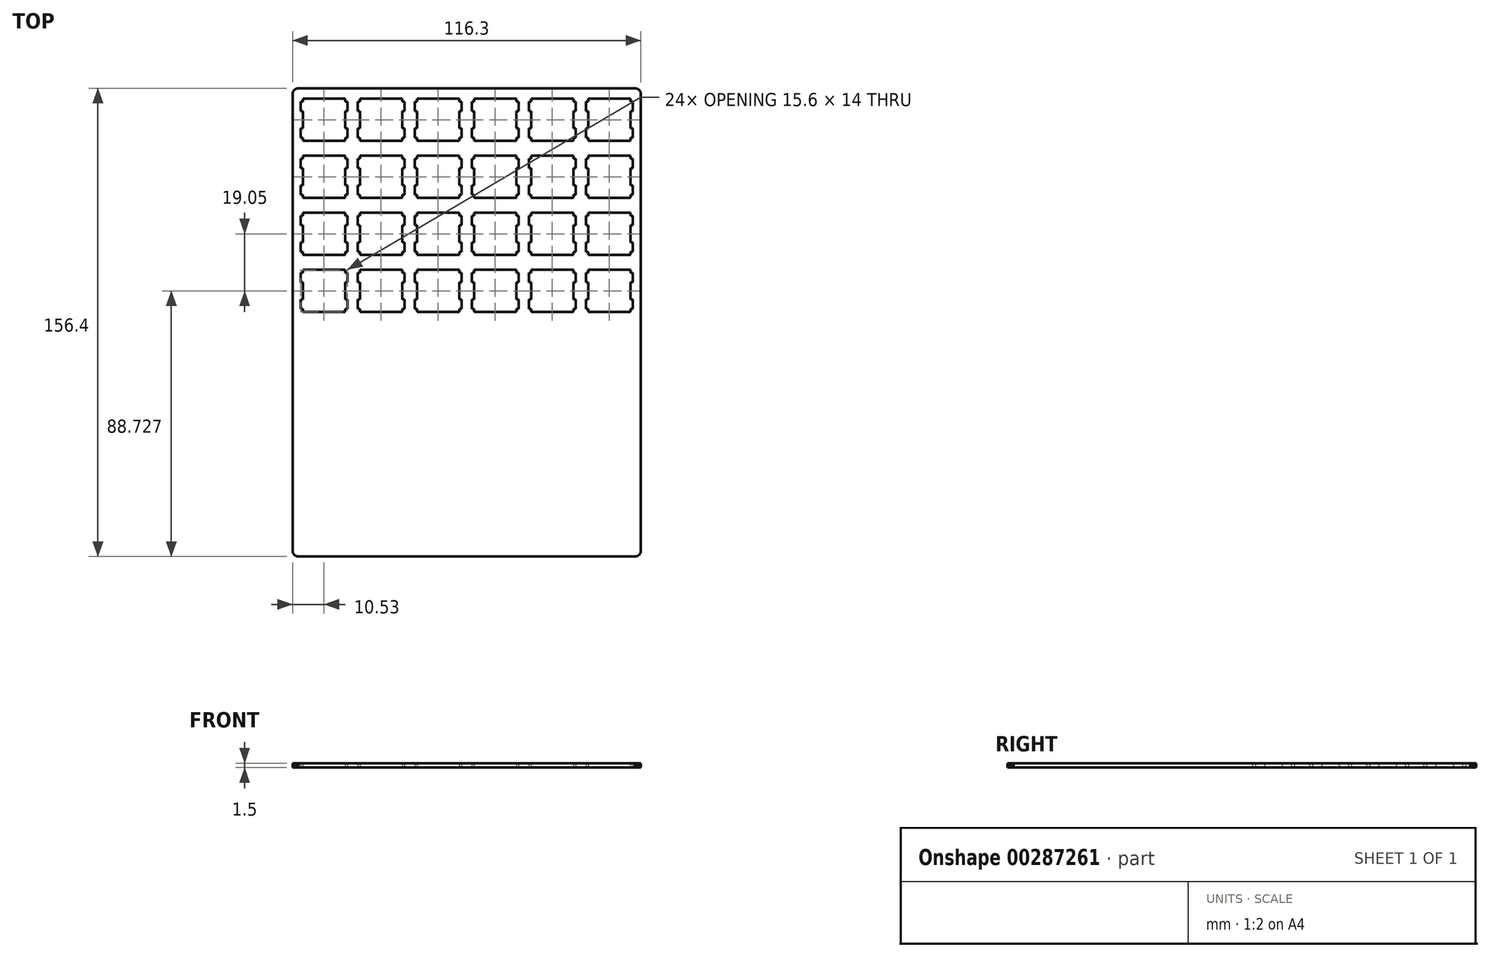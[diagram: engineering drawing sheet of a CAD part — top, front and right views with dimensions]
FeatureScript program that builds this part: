
annotation { "Feature Type Name" : "Feature", "Feature Type Description" : "" }
export const myFeature = defineFeature(function(context is Context, id is Id, definition is map)
    precondition{}
    {
        {
            var Q0;
            Q0=qCreatedBy(makeId("Top.planeOp"),FACE);
            var sketch = newSketch(context, id + "F0", { "sketchPlane" : qUnion([Q0])});
            skLineSegment(sketch, "E0", {"start": v(-39.94, 62.64) * mm, "end": v(-39.94, 61.64) * mm});
            skLineSegment(sketch, "E1", {"start": v(-39.94, 61.64) * mm, "end": v(-53.94, 61.64) * mm});
            skLineSegment(sketch, "E2", {"start": v(-53.94, 61.64) * mm, "end": v(-53.94, 62.64) * mm});
            skLineSegment(sketch, "E3", {"start": v(-53.94, 62.64) * mm, "end": v(-54.74, 62.64) * mm});
            skLineSegment(sketch, "E4", {"start": v(-54.74, 62.64) * mm, "end": v(-54.74, 65.74) * mm});
            skLineSegment(sketch, "E5", {"start": v(-54.74, 65.74) * mm, "end": v(-53.94, 65.74) * mm});
            skLineSegment(sketch, "E6", {"start": v(-53.94, 65.74) * mm, "end": v(-53.94, 71.54) * mm});
            skLineSegment(sketch, "E7", {"start": v(-53.94, 71.54) * mm, "end": v(-54.74, 71.54) * mm});
            skLineSegment(sketch, "E8", {"start": v(-54.74, 71.54) * mm, "end": v(-54.74, 74.64) * mm});
            skLineSegment(sketch, "E9", {"start": v(-54.74, 74.64) * mm, "end": v(-53.94, 74.64) * mm});
            skLineSegment(sketch, "E10", {"start": v(-53.94, 74.64) * mm, "end": v(-53.94, 75.64) * mm});
            skLineSegment(sketch, "E11", {"start": v(-53.94, 75.64) * mm, "end": v(-39.94, 75.64) * mm});
            skLineSegment(sketch, "E12", {"start": v(-39.94, 75.64) * mm, "end": v(-39.94, 74.64) * mm});
            skLineSegment(sketch, "E13", {"start": v(-39.94, 74.64) * mm, "end": v(-39.14, 74.64) * mm});
            skLineSegment(sketch, "E14", {"start": v(-39.14, 74.64) * mm, "end": v(-39.14, 71.54) * mm});
            skLineSegment(sketch, "E15", {"start": v(-39.14, 71.54) * mm, "end": v(-39.94, 71.54) * mm});
            skLineSegment(sketch, "E16", {"start": v(-39.94, 71.54) * mm, "end": v(-39.94, 65.74) * mm});
            skLineSegment(sketch, "E17", {"start": v(-39.94, 65.74) * mm, "end": v(-39.14, 65.74) * mm});
            skLineSegment(sketch, "E18", {"start": v(-39.14, 65.74) * mm, "end": v(-39.14, 62.64) * mm});
            skLineSegment(sketch, "E19", {"start": v(-39.14, 62.64) * mm, "end": v(-39.94, 62.64) * mm});
            skLineSegment(sketch, "E20", {"start": v(-39.94, 43.59) * mm, "end": v(-39.94, 42.59) * mm});
            skLineSegment(sketch, "E21", {"start": v(-39.94, 42.59) * mm, "end": v(-53.94, 42.59) * mm});
            skLineSegment(sketch, "E22", {"start": v(-53.94, 42.59) * mm, "end": v(-53.94, 43.59) * mm});
            skLineSegment(sketch, "E23", {"start": v(-53.94, 43.59) * mm, "end": v(-54.74, 43.59) * mm});
            skLineSegment(sketch, "E24", {"start": v(-54.74, 43.59) * mm, "end": v(-54.74, 46.69) * mm});
            skLineSegment(sketch, "E25", {"start": v(-54.74, 46.69) * mm, "end": v(-53.94, 46.69) * mm});
            skLineSegment(sketch, "E26", {"start": v(-53.94, 46.69) * mm, "end": v(-53.94, 52.49) * mm});
            skLineSegment(sketch, "E27", {"start": v(-53.94, 52.49) * mm, "end": v(-54.74, 52.49) * mm});
            skLineSegment(sketch, "E28", {"start": v(-54.74, 52.49) * mm, "end": v(-54.74, 55.59) * mm});
            skLineSegment(sketch, "E29", {"start": v(-54.74, 55.59) * mm, "end": v(-53.94, 55.59) * mm});
            skLineSegment(sketch, "E30", {"start": v(-53.94, 55.59) * mm, "end": v(-53.94, 56.59) * mm});
            skLineSegment(sketch, "E31", {"start": v(-53.94, 56.59) * mm, "end": v(-39.94, 56.59) * mm});
            skLineSegment(sketch, "E32", {"start": v(-39.94, 56.59) * mm, "end": v(-39.94, 55.59) * mm});
            skLineSegment(sketch, "E33", {"start": v(-39.94, 55.59) * mm, "end": v(-39.14, 55.59) * mm});
            skLineSegment(sketch, "E34", {"start": v(-39.14, 55.59) * mm, "end": v(-39.14, 52.49) * mm});
            skLineSegment(sketch, "E35", {"start": v(-39.14, 52.49) * mm, "end": v(-39.94, 52.49) * mm});
            skLineSegment(sketch, "E36", {"start": v(-39.94, 52.49) * mm, "end": v(-39.94, 46.69) * mm});
            skLineSegment(sketch, "E37", {"start": v(-39.94, 46.69) * mm, "end": v(-39.14, 46.69) * mm});
            skLineSegment(sketch, "E38", {"start": v(-39.14, 46.69) * mm, "end": v(-39.14, 43.59) * mm});
            skLineSegment(sketch, "E39", {"start": v(-39.14, 43.59) * mm, "end": v(-39.94, 43.59) * mm});
            skLineSegment(sketch, "E40", {"start": v(-39.94, 24.54) * mm, "end": v(-39.94, 23.54) * mm});
            skLineSegment(sketch, "E41", {"start": v(-39.94, 23.54) * mm, "end": v(-53.94, 23.54) * mm});
            skLineSegment(sketch, "E42", {"start": v(-53.94, 23.54) * mm, "end": v(-53.94, 24.54) * mm});
            skLineSegment(sketch, "E43", {"start": v(-53.94, 24.54) * mm, "end": v(-54.74, 24.54) * mm});
            skLineSegment(sketch, "E44", {"start": v(-54.74, 24.54) * mm, "end": v(-54.74, 27.64) * mm});
            skLineSegment(sketch, "E45", {"start": v(-54.74, 27.64) * mm, "end": v(-53.94, 27.64) * mm});
            skLineSegment(sketch, "E46", {"start": v(-53.94, 27.64) * mm, "end": v(-53.94, 33.44) * mm});
            skLineSegment(sketch, "E47", {"start": v(-53.94, 33.44) * mm, "end": v(-54.74, 33.44) * mm});
            skLineSegment(sketch, "E48", {"start": v(-54.74, 33.44) * mm, "end": v(-54.74, 36.54) * mm});
            skLineSegment(sketch, "E49", {"start": v(-54.74, 36.54) * mm, "end": v(-53.94, 36.54) * mm});
            skLineSegment(sketch, "E50", {"start": v(-53.94, 36.54) * mm, "end": v(-53.94, 37.54) * mm});
            skLineSegment(sketch, "E51", {"start": v(-53.94, 37.54) * mm, "end": v(-39.94, 37.54) * mm});
            skLineSegment(sketch, "E52", {"start": v(-39.94, 37.54) * mm, "end": v(-39.94, 36.54) * mm});
            skLineSegment(sketch, "E53", {"start": v(-39.94, 36.54) * mm, "end": v(-39.14, 36.54) * mm});
            skLineSegment(sketch, "E54", {"start": v(-39.14, 36.54) * mm, "end": v(-39.14, 33.44) * mm});
            skLineSegment(sketch, "E55", {"start": v(-39.14, 33.44) * mm, "end": v(-39.94, 33.44) * mm});
            skLineSegment(sketch, "E56", {"start": v(-39.94, 33.44) * mm, "end": v(-39.94, 27.64) * mm});
            skLineSegment(sketch, "E57", {"start": v(-39.94, 27.64) * mm, "end": v(-39.14, 27.64) * mm});
            skLineSegment(sketch, "E58", {"start": v(-39.14, 27.64) * mm, "end": v(-39.14, 24.54) * mm});
            skLineSegment(sketch, "E59", {"start": v(-39.14, 24.54) * mm, "end": v(-39.94, 24.54) * mm});
            skLineSegment(sketch, "E60", {"start": v(-39.94, 5.49) * mm, "end": v(-39.94, 4.49) * mm});
            skLineSegment(sketch, "E61", {"start": v(-39.94, 4.49) * mm, "end": v(-53.94, 4.49) * mm});
            skLineSegment(sketch, "E62", {"start": v(-53.94, 4.49) * mm, "end": v(-53.94, 5.49) * mm});
            skLineSegment(sketch, "E63", {"start": v(-53.94, 5.49) * mm, "end": v(-54.74, 5.49) * mm});
            skLineSegment(sketch, "E64", {"start": v(-54.74, 5.49) * mm, "end": v(-54.74, 8.59) * mm});
            skLineSegment(sketch, "E65", {"start": v(-54.74, 8.59) * mm, "end": v(-53.94, 8.59) * mm});
            skLineSegment(sketch, "E66", {"start": v(-53.94, 8.59) * mm, "end": v(-53.94, 14.39) * mm});
            skLineSegment(sketch, "E67", {"start": v(-53.94, 14.39) * mm, "end": v(-54.74, 14.39) * mm});
            skLineSegment(sketch, "E68", {"start": v(-54.74, 14.39) * mm, "end": v(-54.74, 17.49) * mm});
            skLineSegment(sketch, "E69", {"start": v(-54.74, 17.49) * mm, "end": v(-53.94, 17.49) * mm});
            skLineSegment(sketch, "E70", {"start": v(-53.94, 17.49) * mm, "end": v(-53.94, 18.49) * mm});
            skLineSegment(sketch, "E71", {"start": v(-53.94, 18.49) * mm, "end": v(-39.94, 18.49) * mm});
            skLineSegment(sketch, "E72", {"start": v(-39.94, 18.49) * mm, "end": v(-39.94, 17.49) * mm});
            skLineSegment(sketch, "E73", {"start": v(-39.94, 17.49) * mm, "end": v(-39.14, 17.49) * mm});
            skLineSegment(sketch, "E74", {"start": v(-39.14, 17.49) * mm, "end": v(-39.14, 14.39) * mm});
            skLineSegment(sketch, "E75", {"start": v(-39.14, 14.39) * mm, "end": v(-39.94, 14.39) * mm});
            skLineSegment(sketch, "E76", {"start": v(-39.94, 14.39) * mm, "end": v(-39.94, 8.59) * mm});
            skLineSegment(sketch, "E77", {"start": v(-39.94, 8.59) * mm, "end": v(-39.14, 8.59) * mm});
            skLineSegment(sketch, "E78", {"start": v(-39.14, 8.59) * mm, "end": v(-39.14, 5.49) * mm});
            skLineSegment(sketch, "E79", {"start": v(-39.14, 5.49) * mm, "end": v(-39.94, 5.49) * mm});
            skLineSegment(sketch, "E80", {"start": v(-20.9, 62.64) * mm, "end": v(-20.9, 61.64) * mm});
            skLineSegment(sketch, "E81", {"start": v(-20.9, 61.64) * mm, "end": v(-34.9, 61.64) * mm});
            skLineSegment(sketch, "E82", {"start": v(-34.9, 61.64) * mm, "end": v(-34.9, 62.64) * mm});
            skLineSegment(sketch, "E83", {"start": v(-34.9, 62.64) * mm, "end": v(-35.7, 62.64) * mm});
            skLineSegment(sketch, "E84", {"start": v(-35.7, 62.64) * mm, "end": v(-35.7, 65.74) * mm});
            skLineSegment(sketch, "E85", {"start": v(-35.7, 65.74) * mm, "end": v(-34.9, 65.74) * mm});
            skLineSegment(sketch, "E86", {"start": v(-34.9, 65.74) * mm, "end": v(-34.9, 71.54) * mm});
            skLineSegment(sketch, "E87", {"start": v(-34.9, 71.54) * mm, "end": v(-35.7, 71.54) * mm});
            skLineSegment(sketch, "E88", {"start": v(-35.7, 71.54) * mm, "end": v(-35.7, 74.64) * mm});
            skLineSegment(sketch, "E89", {"start": v(-35.7, 74.64) * mm, "end": v(-34.9, 74.64) * mm});
            skLineSegment(sketch, "E90", {"start": v(-34.9, 74.64) * mm, "end": v(-34.9, 75.64) * mm});
            skLineSegment(sketch, "E91", {"start": v(-34.9, 75.64) * mm, "end": v(-20.9, 75.64) * mm});
            skLineSegment(sketch, "E92", {"start": v(-20.9, 75.64) * mm, "end": v(-20.9, 74.64) * mm});
            skLineSegment(sketch, "E93", {"start": v(-20.9, 74.64) * mm, "end": v(-20.1, 74.64) * mm});
            skLineSegment(sketch, "E94", {"start": v(-20.1, 74.64) * mm, "end": v(-20.1, 71.54) * mm});
            skLineSegment(sketch, "E95", {"start": v(-20.1, 71.54) * mm, "end": v(-20.9, 71.54) * mm});
            skLineSegment(sketch, "E96", {"start": v(-20.9, 71.54) * mm, "end": v(-20.9, 65.74) * mm});
            skLineSegment(sketch, "E97", {"start": v(-20.9, 65.74) * mm, "end": v(-20.1, 65.74) * mm});
            skLineSegment(sketch, "E98", {"start": v(-20.1, 65.74) * mm, "end": v(-20.1, 62.64) * mm});
            skLineSegment(sketch, "E99", {"start": v(-20.1, 62.64) * mm, "end": v(-20.9, 62.64) * mm});
            skLineSegment(sketch, "E100", {"start": v(-20.9, 43.59) * mm, "end": v(-20.9, 42.59) * mm});
            skLineSegment(sketch, "E101", {"start": v(-20.9, 42.59) * mm, "end": v(-34.9, 42.59) * mm});
            skLineSegment(sketch, "E102", {"start": v(-34.9, 42.59) * mm, "end": v(-34.9, 43.59) * mm});
            skLineSegment(sketch, "E103", {"start": v(-34.9, 43.59) * mm, "end": v(-35.7, 43.59) * mm});
            skLineSegment(sketch, "E104", {"start": v(-35.7, 43.59) * mm, "end": v(-35.7, 46.69) * mm});
            skLineSegment(sketch, "E105", {"start": v(-35.7, 46.69) * mm, "end": v(-34.9, 46.69) * mm});
            skLineSegment(sketch, "E106", {"start": v(-34.9, 46.69) * mm, "end": v(-34.9, 52.49) * mm});
            skLineSegment(sketch, "E107", {"start": v(-34.9, 52.49) * mm, "end": v(-35.7, 52.49) * mm});
            skLineSegment(sketch, "E108", {"start": v(-35.7, 52.49) * mm, "end": v(-35.7, 55.59) * mm});
            skLineSegment(sketch, "E109", {"start": v(-35.7, 55.59) * mm, "end": v(-34.9, 55.59) * mm});
            skLineSegment(sketch, "E110", {"start": v(-34.9, 55.59) * mm, "end": v(-34.9, 56.59) * mm});
            skLineSegment(sketch, "E111", {"start": v(-34.9, 56.59) * mm, "end": v(-20.9, 56.59) * mm});
            skLineSegment(sketch, "E112", {"start": v(-20.9, 56.59) * mm, "end": v(-20.9, 55.59) * mm});
            skLineSegment(sketch, "E113", {"start": v(-20.9, 55.59) * mm, "end": v(-20.1, 55.59) * mm});
            skLineSegment(sketch, "E114", {"start": v(-20.1, 55.59) * mm, "end": v(-20.1, 52.49) * mm});
            skLineSegment(sketch, "E115", {"start": v(-20.1, 52.49) * mm, "end": v(-20.9, 52.49) * mm});
            skLineSegment(sketch, "E116", {"start": v(-20.9, 52.49) * mm, "end": v(-20.9, 46.69) * mm});
            skLineSegment(sketch, "E117", {"start": v(-20.9, 46.69) * mm, "end": v(-20.1, 46.69) * mm});
            skLineSegment(sketch, "E118", {"start": v(-20.1, 46.69) * mm, "end": v(-20.1, 43.59) * mm});
            skLineSegment(sketch, "E119", {"start": v(-20.1, 43.59) * mm, "end": v(-20.9, 43.59) * mm});
            skLineSegment(sketch, "E120", {"start": v(-20.9, 24.54) * mm, "end": v(-20.9, 23.54) * mm});
            skLineSegment(sketch, "E121", {"start": v(-20.9, 23.54) * mm, "end": v(-34.9, 23.54) * mm});
            skLineSegment(sketch, "E122", {"start": v(-34.9, 23.54) * mm, "end": v(-34.9, 24.54) * mm});
            skLineSegment(sketch, "E123", {"start": v(-34.9, 24.54) * mm, "end": v(-35.7, 24.54) * mm});
            skLineSegment(sketch, "E124", {"start": v(-35.7, 24.54) * mm, "end": v(-35.7, 27.64) * mm});
            skLineSegment(sketch, "E125", {"start": v(-35.7, 27.64) * mm, "end": v(-34.9, 27.64) * mm});
            skLineSegment(sketch, "E126", {"start": v(-34.9, 27.64) * mm, "end": v(-34.9, 33.44) * mm});
            skLineSegment(sketch, "E127", {"start": v(-34.9, 33.44) * mm, "end": v(-35.7, 33.44) * mm});
            skLineSegment(sketch, "E128", {"start": v(-35.7, 33.44) * mm, "end": v(-35.7, 36.54) * mm});
            skLineSegment(sketch, "E129", {"start": v(-35.7, 36.54) * mm, "end": v(-34.9, 36.54) * mm});
            skLineSegment(sketch, "E130", {"start": v(-34.9, 36.54) * mm, "end": v(-34.9, 37.54) * mm});
            skLineSegment(sketch, "E131", {"start": v(-34.9, 37.54) * mm, "end": v(-20.9, 37.54) * mm});
            skLineSegment(sketch, "E132", {"start": v(-20.9, 37.54) * mm, "end": v(-20.9, 36.54) * mm});
            skLineSegment(sketch, "E133", {"start": v(-20.9, 36.54) * mm, "end": v(-20.1, 36.54) * mm});
            skLineSegment(sketch, "E134", {"start": v(-20.1, 36.54) * mm, "end": v(-20.1, 33.44) * mm});
            skLineSegment(sketch, "E135", {"start": v(-20.1, 33.44) * mm, "end": v(-20.9, 33.44) * mm});
            skLineSegment(sketch, "E136", {"start": v(-20.9, 33.44) * mm, "end": v(-20.9, 27.64) * mm});
            skLineSegment(sketch, "E137", {"start": v(-20.9, 27.64) * mm, "end": v(-20.1, 27.64) * mm});
            skLineSegment(sketch, "E138", {"start": v(-20.1, 27.64) * mm, "end": v(-20.1, 24.54) * mm});
            skLineSegment(sketch, "E139", {"start": v(-20.1, 24.54) * mm, "end": v(-20.9, 24.54) * mm});
            skLineSegment(sketch, "E140", {"start": v(-20.9, 5.49) * mm, "end": v(-20.9, 4.49) * mm});
            skLineSegment(sketch, "E141", {"start": v(-20.9, 4.49) * mm, "end": v(-34.9, 4.49) * mm});
            skLineSegment(sketch, "E142", {"start": v(-34.9, 4.49) * mm, "end": v(-34.9, 5.49) * mm});
            skLineSegment(sketch, "E143", {"start": v(-34.9, 5.49) * mm, "end": v(-35.7, 5.49) * mm});
            skLineSegment(sketch, "E144", {"start": v(-35.7, 5.49) * mm, "end": v(-35.7, 8.59) * mm});
            skLineSegment(sketch, "E145", {"start": v(-35.7, 8.59) * mm, "end": v(-34.9, 8.59) * mm});
            skLineSegment(sketch, "E146", {"start": v(-34.9, 8.59) * mm, "end": v(-34.9, 14.39) * mm});
            skLineSegment(sketch, "E147", {"start": v(-34.9, 14.39) * mm, "end": v(-35.7, 14.39) * mm});
            skLineSegment(sketch, "E148", {"start": v(-35.7, 14.39) * mm, "end": v(-35.7, 17.49) * mm});
            skLineSegment(sketch, "E149", {"start": v(-35.7, 17.49) * mm, "end": v(-34.9, 17.49) * mm});
            skLineSegment(sketch, "E150", {"start": v(-34.9, 17.49) * mm, "end": v(-34.9, 18.49) * mm});
            skLineSegment(sketch, "E151", {"start": v(-34.9, 18.49) * mm, "end": v(-20.9, 18.49) * mm});
            skLineSegment(sketch, "E152", {"start": v(-20.9, 18.49) * mm, "end": v(-20.9, 17.49) * mm});
            skLineSegment(sketch, "E153", {"start": v(-20.9, 17.49) * mm, "end": v(-20.1, 17.49) * mm});
            skLineSegment(sketch, "E154", {"start": v(-20.1, 17.49) * mm, "end": v(-20.1, 14.39) * mm});
            skLineSegment(sketch, "E155", {"start": v(-20.1, 14.39) * mm, "end": v(-20.9, 14.39) * mm});
            skLineSegment(sketch, "E156", {"start": v(-20.9, 14.39) * mm, "end": v(-20.9, 8.59) * mm});
            skLineSegment(sketch, "E157", {"start": v(-20.9, 8.59) * mm, "end": v(-20.1, 8.59) * mm});
            skLineSegment(sketch, "E158", {"start": v(-20.1, 8.59) * mm, "end": v(-20.1, 5.49) * mm});
            skLineSegment(sketch, "E159", {"start": v(-20.1, 5.49) * mm, "end": v(-20.9, 5.49) * mm});
            skLineSegment(sketch, "E160", {"start": v(-1.84, 62.64) * mm, "end": v(-1.84, 61.64) * mm});
            skLineSegment(sketch, "E161", {"start": v(-1.84, 61.64) * mm, "end": v(-15.84, 61.64) * mm});
            skLineSegment(sketch, "E162", {"start": v(-15.84, 61.64) * mm, "end": v(-15.84, 62.64) * mm});
            skLineSegment(sketch, "E163", {"start": v(-15.84, 62.64) * mm, "end": v(-16.64, 62.64) * mm});
            skLineSegment(sketch, "E164", {"start": v(-16.64, 62.64) * mm, "end": v(-16.64, 65.74) * mm});
            skLineSegment(sketch, "E165", {"start": v(-16.64, 65.74) * mm, "end": v(-15.84, 65.74) * mm});
            skLineSegment(sketch, "E166", {"start": v(-15.84, 65.74) * mm, "end": v(-15.84, 71.54) * mm});
            skLineSegment(sketch, "E167", {"start": v(-15.84, 71.54) * mm, "end": v(-16.64, 71.54) * mm});
            skLineSegment(sketch, "E168", {"start": v(-16.64, 71.54) * mm, "end": v(-16.64, 74.64) * mm});
            skLineSegment(sketch, "E169", {"start": v(-16.64, 74.64) * mm, "end": v(-15.84, 74.64) * mm});
            skLineSegment(sketch, "E170", {"start": v(-15.84, 74.64) * mm, "end": v(-15.84, 75.64) * mm});
            skLineSegment(sketch, "E171", {"start": v(-15.84, 75.64) * mm, "end": v(-1.84, 75.64) * mm});
            skLineSegment(sketch, "E172", {"start": v(-1.84, 75.64) * mm, "end": v(-1.84, 74.64) * mm});
            skLineSegment(sketch, "E173", {"start": v(-1.84, 74.64) * mm, "end": v(-1.04, 74.64) * mm});
            skLineSegment(sketch, "E174", {"start": v(-1.04, 74.64) * mm, "end": v(-1.04, 71.54) * mm});
            skLineSegment(sketch, "E175", {"start": v(-1.04, 71.54) * mm, "end": v(-1.84, 71.54) * mm});
            skLineSegment(sketch, "E176", {"start": v(-1.84, 71.54) * mm, "end": v(-1.84, 65.74) * mm});
            skLineSegment(sketch, "E177", {"start": v(-1.84, 65.74) * mm, "end": v(-1.04, 65.74) * mm});
            skLineSegment(sketch, "E178", {"start": v(-1.04, 65.74) * mm, "end": v(-1.04, 62.64) * mm});
            skLineSegment(sketch, "E179", {"start": v(-1.04, 62.64) * mm, "end": v(-1.84, 62.64) * mm});
            skLineSegment(sketch, "E180", {"start": v(-1.84, 43.59) * mm, "end": v(-1.84, 42.59) * mm});
            skLineSegment(sketch, "E181", {"start": v(-1.84, 42.59) * mm, "end": v(-15.84, 42.59) * mm});
            skLineSegment(sketch, "E182", {"start": v(-15.84, 42.59) * mm, "end": v(-15.84, 43.59) * mm});
            skLineSegment(sketch, "E183", {"start": v(-15.84, 43.59) * mm, "end": v(-16.64, 43.59) * mm});
            skLineSegment(sketch, "E184", {"start": v(-16.64, 43.59) * mm, "end": v(-16.64, 46.69) * mm});
            skLineSegment(sketch, "E185", {"start": v(-16.64, 46.69) * mm, "end": v(-15.84, 46.69) * mm});
            skLineSegment(sketch, "E186", {"start": v(-15.84, 46.69) * mm, "end": v(-15.84, 52.49) * mm});
            skLineSegment(sketch, "E187", {"start": v(-15.84, 52.49) * mm, "end": v(-16.64, 52.49) * mm});
            skLineSegment(sketch, "E188", {"start": v(-16.64, 52.49) * mm, "end": v(-16.64, 55.59) * mm});
            skLineSegment(sketch, "E189", {"start": v(-16.64, 55.59) * mm, "end": v(-15.84, 55.59) * mm});
            skLineSegment(sketch, "E190", {"start": v(-15.84, 55.59) * mm, "end": v(-15.84, 56.59) * mm});
            skLineSegment(sketch, "E191", {"start": v(-15.84, 56.59) * mm, "end": v(-1.84, 56.59) * mm});
            skLineSegment(sketch, "E192", {"start": v(-1.84, 56.59) * mm, "end": v(-1.84, 55.59) * mm});
            skLineSegment(sketch, "E193", {"start": v(-1.84, 55.59) * mm, "end": v(-1.04, 55.59) * mm});
            skLineSegment(sketch, "E194", {"start": v(-1.04, 55.59) * mm, "end": v(-1.04, 52.49) * mm});
            skLineSegment(sketch, "E195", {"start": v(-1.04, 52.49) * mm, "end": v(-1.84, 52.49) * mm});
            skLineSegment(sketch, "E196", {"start": v(-1.84, 52.49) * mm, "end": v(-1.84, 46.69) * mm});
            skLineSegment(sketch, "E197", {"start": v(-1.84, 46.69) * mm, "end": v(-1.04, 46.69) * mm});
            skLineSegment(sketch, "E198", {"start": v(-1.04, 46.69) * mm, "end": v(-1.04, 43.59) * mm});
            skLineSegment(sketch, "E199", {"start": v(-1.04, 43.59) * mm, "end": v(-1.84, 43.59) * mm});
            skLineSegment(sketch, "E200", {"start": v(-1.84, 24.54) * mm, "end": v(-1.84, 23.54) * mm});
            skLineSegment(sketch, "E201", {"start": v(-1.84, 23.54) * mm, "end": v(-15.84, 23.54) * mm});
            skLineSegment(sketch, "E202", {"start": v(-15.84, 23.54) * mm, "end": v(-15.84, 24.54) * mm});
            skLineSegment(sketch, "E203", {"start": v(-15.84, 24.54) * mm, "end": v(-16.64, 24.54) * mm});
            skLineSegment(sketch, "E204", {"start": v(-16.64, 24.54) * mm, "end": v(-16.64, 27.64) * mm});
            skLineSegment(sketch, "E205", {"start": v(-16.64, 27.64) * mm, "end": v(-15.84, 27.64) * mm});
            skLineSegment(sketch, "E206", {"start": v(-15.84, 27.64) * mm, "end": v(-15.84, 33.44) * mm});
            skLineSegment(sketch, "E207", {"start": v(-15.84, 33.44) * mm, "end": v(-16.64, 33.44) * mm});
            skLineSegment(sketch, "E208", {"start": v(-16.64, 33.44) * mm, "end": v(-16.64, 36.54) * mm});
            skLineSegment(sketch, "E209", {"start": v(-16.64, 36.54) * mm, "end": v(-15.84, 36.54) * mm});
            skLineSegment(sketch, "E210", {"start": v(-15.84, 36.54) * mm, "end": v(-15.84, 37.54) * mm});
            skLineSegment(sketch, "E211", {"start": v(-15.84, 37.54) * mm, "end": v(-1.84, 37.54) * mm});
            skLineSegment(sketch, "E212", {"start": v(-1.84, 37.54) * mm, "end": v(-1.84, 36.54) * mm});
            skLineSegment(sketch, "E213", {"start": v(-1.84, 36.54) * mm, "end": v(-1.04, 36.54) * mm});
            skLineSegment(sketch, "E214", {"start": v(-1.04, 36.54) * mm, "end": v(-1.04, 33.44) * mm});
            skLineSegment(sketch, "E215", {"start": v(-1.04, 33.44) * mm, "end": v(-1.84, 33.44) * mm});
            skLineSegment(sketch, "E216", {"start": v(-1.84, 33.44) * mm, "end": v(-1.84, 27.64) * mm});
            skLineSegment(sketch, "E217", {"start": v(-1.84, 27.64) * mm, "end": v(-1.04, 27.64) * mm});
            skLineSegment(sketch, "E218", {"start": v(-1.04, 27.64) * mm, "end": v(-1.04, 24.54) * mm});
            skLineSegment(sketch, "E219", {"start": v(-1.04, 24.54) * mm, "end": v(-1.84, 24.54) * mm});
            skLineSegment(sketch, "E220", {"start": v(-1.84, 5.49) * mm, "end": v(-1.84, 4.49) * mm});
            skLineSegment(sketch, "E221", {"start": v(-1.84, 4.49) * mm, "end": v(-15.84, 4.49) * mm});
            skLineSegment(sketch, "E222", {"start": v(-15.84, 4.49) * mm, "end": v(-15.84, 5.49) * mm});
            skLineSegment(sketch, "E223", {"start": v(-15.84, 5.49) * mm, "end": v(-16.64, 5.49) * mm});
            skLineSegment(sketch, "E224", {"start": v(-16.64, 5.49) * mm, "end": v(-16.64, 8.59) * mm});
            skLineSegment(sketch, "E225", {"start": v(-16.64, 8.59) * mm, "end": v(-15.84, 8.59) * mm});
            skLineSegment(sketch, "E226", {"start": v(-15.84, 8.59) * mm, "end": v(-15.84, 14.39) * mm});
            skLineSegment(sketch, "E227", {"start": v(-15.84, 14.39) * mm, "end": v(-16.64, 14.39) * mm});
            skLineSegment(sketch, "E228", {"start": v(-16.64, 14.39) * mm, "end": v(-16.64, 17.49) * mm});
            skLineSegment(sketch, "E229", {"start": v(-16.64, 17.49) * mm, "end": v(-15.84, 17.49) * mm});
            skLineSegment(sketch, "E230", {"start": v(-15.84, 17.49) * mm, "end": v(-15.84, 18.49) * mm});
            skLineSegment(sketch, "E231", {"start": v(-15.84, 18.49) * mm, "end": v(-1.84, 18.49) * mm});
            skLineSegment(sketch, "E232", {"start": v(-1.84, 18.49) * mm, "end": v(-1.84, 17.49) * mm});
            skLineSegment(sketch, "E233", {"start": v(-1.84, 17.49) * mm, "end": v(-1.04, 17.49) * mm});
            skLineSegment(sketch, "E234", {"start": v(-1.04, 17.49) * mm, "end": v(-1.04, 14.39) * mm});
            skLineSegment(sketch, "E235", {"start": v(-1.04, 14.39) * mm, "end": v(-1.84, 14.39) * mm});
            skLineSegment(sketch, "E236", {"start": v(-1.84, 14.39) * mm, "end": v(-1.84, 8.59) * mm});
            skLineSegment(sketch, "E237", {"start": v(-1.84, 8.59) * mm, "end": v(-1.04, 8.59) * mm});
            skLineSegment(sketch, "E238", {"start": v(-1.04, 8.59) * mm, "end": v(-1.04, 5.49) * mm});
            skLineSegment(sketch, "E239", {"start": v(-1.04, 5.49) * mm, "end": v(-1.84, 5.49) * mm});
            skLineSegment(sketch, "E240", {"start": v(17.2, 62.64) * mm, "end": v(17.2, 61.64) * mm});
            skLineSegment(sketch, "E241", {"start": v(17.2, 61.64) * mm, "end": v(3.2, 61.64) * mm});
            skLineSegment(sketch, "E242", {"start": v(3.2, 61.64) * mm, "end": v(3.2, 62.64) * mm});
            skLineSegment(sketch, "E243", {"start": v(3.2, 62.64) * mm, "end": v(2.4, 62.64) * mm});
            skLineSegment(sketch, "E244", {"start": v(2.4, 62.64) * mm, "end": v(2.4, 65.74) * mm});
            skLineSegment(sketch, "E245", {"start": v(2.4, 65.74) * mm, "end": v(3.2, 65.74) * mm});
            skLineSegment(sketch, "E246", {"start": v(3.2, 65.74) * mm, "end": v(3.2, 71.54) * mm});
            skLineSegment(sketch, "E247", {"start": v(3.2, 71.54) * mm, "end": v(2.4, 71.54) * mm});
            skLineSegment(sketch, "E248", {"start": v(2.4, 71.54) * mm, "end": v(2.4, 74.64) * mm});
            skLineSegment(sketch, "E249", {"start": v(2.4, 74.64) * mm, "end": v(3.2, 74.64) * mm});
            skLineSegment(sketch, "E250", {"start": v(3.2, 74.64) * mm, "end": v(3.2, 75.64) * mm});
            skLineSegment(sketch, "E251", {"start": v(3.2, 75.64) * mm, "end": v(17.2, 75.64) * mm});
            skLineSegment(sketch, "E252", {"start": v(17.2, 75.64) * mm, "end": v(17.2, 74.64) * mm});
            skLineSegment(sketch, "E253", {"start": v(17.2, 74.64) * mm, "end": v(18, 74.64) * mm});
            skLineSegment(sketch, "E254", {"start": v(18, 74.64) * mm, "end": v(18, 71.54) * mm});
            skLineSegment(sketch, "E255", {"start": v(18, 71.54) * mm, "end": v(17.2, 71.54) * mm});
            skLineSegment(sketch, "E256", {"start": v(17.2, 71.54) * mm, "end": v(17.2, 65.74) * mm});
            skLineSegment(sketch, "E257", {"start": v(17.2, 65.74) * mm, "end": v(18, 65.74) * mm});
            skLineSegment(sketch, "E258", {"start": v(18, 65.74) * mm, "end": v(18, 62.64) * mm});
            skLineSegment(sketch, "E259", {"start": v(18, 62.64) * mm, "end": v(17.2, 62.64) * mm});
            skLineSegment(sketch, "E260", {"start": v(17.2, 43.59) * mm, "end": v(17.2, 42.59) * mm});
            skLineSegment(sketch, "E261", {"start": v(17.2, 42.59) * mm, "end": v(3.2, 42.59) * mm});
            skLineSegment(sketch, "E262", {"start": v(3.2, 42.59) * mm, "end": v(3.2, 43.59) * mm});
            skLineSegment(sketch, "E263", {"start": v(3.2, 43.59) * mm, "end": v(2.4, 43.59) * mm});
            skLineSegment(sketch, "E264", {"start": v(2.4, 43.59) * mm, "end": v(2.4, 46.69) * mm});
            skLineSegment(sketch, "E265", {"start": v(2.4, 46.69) * mm, "end": v(3.2, 46.69) * mm});
            skLineSegment(sketch, "E266", {"start": v(3.2, 46.69) * mm, "end": v(3.2, 52.49) * mm});
            skLineSegment(sketch, "E267", {"start": v(3.2, 52.49) * mm, "end": v(2.4, 52.49) * mm});
            skLineSegment(sketch, "E268", {"start": v(2.4, 52.49) * mm, "end": v(2.4, 55.59) * mm});
            skLineSegment(sketch, "E269", {"start": v(2.4, 55.59) * mm, "end": v(3.2, 55.59) * mm});
            skLineSegment(sketch, "E270", {"start": v(3.2, 55.59) * mm, "end": v(3.2, 56.59) * mm});
            skLineSegment(sketch, "E271", {"start": v(3.2, 56.59) * mm, "end": v(17.2, 56.59) * mm});
            skLineSegment(sketch, "E272", {"start": v(17.2, 56.59) * mm, "end": v(17.2, 55.59) * mm});
            skLineSegment(sketch, "E273", {"start": v(17.2, 55.59) * mm, "end": v(18, 55.59) * mm});
            skLineSegment(sketch, "E274", {"start": v(18, 55.59) * mm, "end": v(18, 52.49) * mm});
            skLineSegment(sketch, "E275", {"start": v(18, 52.49) * mm, "end": v(17.2, 52.49) * mm});
            skLineSegment(sketch, "E276", {"start": v(17.2, 52.49) * mm, "end": v(17.2, 46.69) * mm});
            skLineSegment(sketch, "E277", {"start": v(17.2, 46.69) * mm, "end": v(18, 46.69) * mm});
            skLineSegment(sketch, "E278", {"start": v(18, 46.69) * mm, "end": v(18, 43.59) * mm});
            skLineSegment(sketch, "E279", {"start": v(18, 43.59) * mm, "end": v(17.2, 43.59) * mm});
            skLineSegment(sketch, "E280", {"start": v(17.2, 24.54) * mm, "end": v(17.2, 23.54) * mm});
            skLineSegment(sketch, "E281", {"start": v(17.2, 23.54) * mm, "end": v(3.2, 23.54) * mm});
            skLineSegment(sketch, "E282", {"start": v(3.2, 23.54) * mm, "end": v(3.2, 24.54) * mm});
            skLineSegment(sketch, "E283", {"start": v(3.2, 24.54) * mm, "end": v(2.4, 24.54) * mm});
            skLineSegment(sketch, "E284", {"start": v(2.4, 24.54) * mm, "end": v(2.4, 27.64) * mm});
            skLineSegment(sketch, "E285", {"start": v(2.4, 27.64) * mm, "end": v(3.2, 27.64) * mm});
            skLineSegment(sketch, "E286", {"start": v(3.2, 27.64) * mm, "end": v(3.2, 33.44) * mm});
            skLineSegment(sketch, "E287", {"start": v(3.2, 33.44) * mm, "end": v(2.4, 33.44) * mm});
            skLineSegment(sketch, "E288", {"start": v(2.4, 33.44) * mm, "end": v(2.4, 36.54) * mm});
            skLineSegment(sketch, "E289", {"start": v(2.4, 36.54) * mm, "end": v(3.2, 36.54) * mm});
            skLineSegment(sketch, "E290", {"start": v(3.2, 36.54) * mm, "end": v(3.2, 37.54) * mm});
            skLineSegment(sketch, "E291", {"start": v(3.2, 37.54) * mm, "end": v(17.2, 37.54) * mm});
            skLineSegment(sketch, "E292", {"start": v(17.2, 37.54) * mm, "end": v(17.2, 36.54) * mm});
            skLineSegment(sketch, "E293", {"start": v(17.2, 36.54) * mm, "end": v(18, 36.54) * mm});
            skLineSegment(sketch, "E294", {"start": v(18, 36.54) * mm, "end": v(18, 33.44) * mm});
            skLineSegment(sketch, "E295", {"start": v(18, 33.44) * mm, "end": v(17.2, 33.44) * mm});
            skLineSegment(sketch, "E296", {"start": v(17.2, 33.44) * mm, "end": v(17.2, 27.64) * mm});
            skLineSegment(sketch, "E297", {"start": v(17.2, 27.64) * mm, "end": v(18, 27.64) * mm});
            skLineSegment(sketch, "E298", {"start": v(18, 27.64) * mm, "end": v(18, 24.54) * mm});
            skLineSegment(sketch, "E299", {"start": v(18, 24.54) * mm, "end": v(17.2, 24.54) * mm});
            skLineSegment(sketch, "E300", {"start": v(17.2, 5.49) * mm, "end": v(17.2, 4.49) * mm});
            skLineSegment(sketch, "E301", {"start": v(17.2, 4.49) * mm, "end": v(3.2, 4.49) * mm});
            skLineSegment(sketch, "E302", {"start": v(3.2, 4.49) * mm, "end": v(3.2, 5.49) * mm});
            skLineSegment(sketch, "E303", {"start": v(3.2, 5.49) * mm, "end": v(2.4, 5.49) * mm});
            skLineSegment(sketch, "E304", {"start": v(2.4, 5.49) * mm, "end": v(2.4, 8.59) * mm});
            skLineSegment(sketch, "E305", {"start": v(2.4, 8.59) * mm, "end": v(3.2, 8.59) * mm});
            skLineSegment(sketch, "E306", {"start": v(3.2, 8.59) * mm, "end": v(3.2, 14.39) * mm});
            skLineSegment(sketch, "E307", {"start": v(3.2, 14.39) * mm, "end": v(2.4, 14.39) * mm});
            skLineSegment(sketch, "E308", {"start": v(2.4, 14.39) * mm, "end": v(2.4, 17.49) * mm});
            skLineSegment(sketch, "E309", {"start": v(2.4, 17.49) * mm, "end": v(3.2, 17.49) * mm});
            skLineSegment(sketch, "E310", {"start": v(3.2, 17.49) * mm, "end": v(3.2, 18.49) * mm});
            skLineSegment(sketch, "E311", {"start": v(3.2, 18.49) * mm, "end": v(17.2, 18.49) * mm});
            skLineSegment(sketch, "E312", {"start": v(17.2, 18.49) * mm, "end": v(17.2, 17.49) * mm});
            skLineSegment(sketch, "E313", {"start": v(17.2, 17.49) * mm, "end": v(18, 17.49) * mm});
            skLineSegment(sketch, "E314", {"start": v(18, 17.49) * mm, "end": v(18, 14.39) * mm});
            skLineSegment(sketch, "E315", {"start": v(18, 14.39) * mm, "end": v(17.2, 14.39) * mm});
            skLineSegment(sketch, "E316", {"start": v(17.2, 14.39) * mm, "end": v(17.2, 8.59) * mm});
            skLineSegment(sketch, "E317", {"start": v(17.2, 8.59) * mm, "end": v(18, 8.59) * mm});
            skLineSegment(sketch, "E318", {"start": v(18, 8.59) * mm, "end": v(18, 5.49) * mm});
            skLineSegment(sketch, "E319", {"start": v(18, 5.49) * mm, "end": v(17.2, 5.49) * mm});
            skLineSegment(sketch, "E320", {"start": v(36.26, 62.64) * mm, "end": v(36.26, 61.64) * mm});
            skLineSegment(sketch, "E321", {"start": v(36.26, 61.64) * mm, "end": v(22.26, 61.64) * mm});
            skLineSegment(sketch, "E322", {"start": v(22.26, 61.64) * mm, "end": v(22.26, 62.64) * mm});
            skLineSegment(sketch, "E323", {"start": v(22.26, 62.64) * mm, "end": v(21.46, 62.64) * mm});
            skLineSegment(sketch, "E324", {"start": v(21.46, 62.64) * mm, "end": v(21.46, 65.74) * mm});
            skLineSegment(sketch, "E325", {"start": v(21.46, 65.74) * mm, "end": v(22.26, 65.74) * mm});
            skLineSegment(sketch, "E326", {"start": v(22.26, 65.74) * mm, "end": v(22.26, 71.54) * mm});
            skLineSegment(sketch, "E327", {"start": v(22.26, 71.54) * mm, "end": v(21.46, 71.54) * mm});
            skLineSegment(sketch, "E328", {"start": v(21.46, 71.54) * mm, "end": v(21.46, 74.64) * mm});
            skLineSegment(sketch, "E329", {"start": v(21.46, 74.64) * mm, "end": v(22.26, 74.64) * mm});
            skLineSegment(sketch, "E330", {"start": v(22.26, 74.64) * mm, "end": v(22.26, 75.64) * mm});
            skLineSegment(sketch, "E331", {"start": v(22.26, 75.64) * mm, "end": v(36.26, 75.64) * mm});
            skLineSegment(sketch, "E332", {"start": v(36.26, 75.64) * mm, "end": v(36.26, 74.64) * mm});
            skLineSegment(sketch, "E333", {"start": v(36.26, 74.64) * mm, "end": v(37.06, 74.64) * mm});
            skLineSegment(sketch, "E334", {"start": v(37.06, 74.64) * mm, "end": v(37.06, 71.54) * mm});
            skLineSegment(sketch, "E335", {"start": v(37.06, 71.54) * mm, "end": v(36.26, 71.54) * mm});
            skLineSegment(sketch, "E336", {"start": v(36.26, 71.54) * mm, "end": v(36.26, 65.74) * mm});
            skLineSegment(sketch, "E337", {"start": v(36.26, 65.74) * mm, "end": v(37.06, 65.74) * mm});
            skLineSegment(sketch, "E338", {"start": v(37.06, 65.74) * mm, "end": v(37.06, 62.64) * mm});
            skLineSegment(sketch, "E339", {"start": v(37.06, 62.64) * mm, "end": v(36.26, 62.64) * mm});
            skLineSegment(sketch, "E340", {"start": v(36.26, 43.59) * mm, "end": v(36.26, 42.59) * mm});
            skLineSegment(sketch, "E341", {"start": v(36.26, 42.59) * mm, "end": v(22.26, 42.59) * mm});
            skLineSegment(sketch, "E342", {"start": v(22.26, 42.59) * mm, "end": v(22.26, 43.59) * mm});
            skLineSegment(sketch, "E343", {"start": v(22.26, 43.59) * mm, "end": v(21.46, 43.59) * mm});
            skLineSegment(sketch, "E344", {"start": v(21.46, 43.59) * mm, "end": v(21.46, 46.69) * mm});
            skLineSegment(sketch, "E345", {"start": v(21.46, 46.69) * mm, "end": v(22.26, 46.69) * mm});
            skLineSegment(sketch, "E346", {"start": v(22.26, 46.69) * mm, "end": v(22.26, 52.49) * mm});
            skLineSegment(sketch, "E347", {"start": v(22.26, 52.49) * mm, "end": v(21.46, 52.49) * mm});
            skLineSegment(sketch, "E348", {"start": v(21.46, 52.49) * mm, "end": v(21.46, 55.59) * mm});
            skLineSegment(sketch, "E349", {"start": v(21.46, 55.59) * mm, "end": v(22.26, 55.59) * mm});
            skLineSegment(sketch, "E350", {"start": v(22.26, 55.59) * mm, "end": v(22.26, 56.59) * mm});
            skLineSegment(sketch, "E351", {"start": v(22.26, 56.59) * mm, "end": v(36.26, 56.59) * mm});
            skLineSegment(sketch, "E352", {"start": v(36.26, 56.59) * mm, "end": v(36.26, 55.59) * mm});
            skLineSegment(sketch, "E353", {"start": v(36.26, 55.59) * mm, "end": v(37.06, 55.59) * mm});
            skLineSegment(sketch, "E354", {"start": v(37.06, 55.59) * mm, "end": v(37.06, 52.49) * mm});
            skLineSegment(sketch, "E355", {"start": v(37.06, 52.49) * mm, "end": v(36.26, 52.49) * mm});
            skLineSegment(sketch, "E356", {"start": v(36.26, 52.49) * mm, "end": v(36.26, 46.69) * mm});
            skLineSegment(sketch, "E357", {"start": v(36.26, 46.69) * mm, "end": v(37.06, 46.69) * mm});
            skLineSegment(sketch, "E358", {"start": v(37.06, 46.69) * mm, "end": v(37.06, 43.59) * mm});
            skLineSegment(sketch, "E359", {"start": v(37.06, 43.59) * mm, "end": v(36.26, 43.59) * mm});
            skLineSegment(sketch, "E360", {"start": v(36.26, 24.54) * mm, "end": v(36.26, 23.54) * mm});
            skLineSegment(sketch, "E361", {"start": v(36.26, 23.54) * mm, "end": v(22.26, 23.54) * mm});
            skLineSegment(sketch, "E362", {"start": v(22.26, 23.54) * mm, "end": v(22.26, 24.54) * mm});
            skLineSegment(sketch, "E363", {"start": v(22.26, 24.54) * mm, "end": v(21.46, 24.54) * mm});
            skLineSegment(sketch, "E364", {"start": v(21.46, 24.54) * mm, "end": v(21.46, 27.64) * mm});
            skLineSegment(sketch, "E365", {"start": v(21.46, 27.64) * mm, "end": v(22.26, 27.64) * mm});
            skLineSegment(sketch, "E366", {"start": v(22.26, 27.64) * mm, "end": v(22.26, 33.44) * mm});
            skLineSegment(sketch, "E367", {"start": v(22.26, 33.44) * mm, "end": v(21.46, 33.44) * mm});
            skLineSegment(sketch, "E368", {"start": v(21.46, 33.44) * mm, "end": v(21.46, 36.54) * mm});
            skLineSegment(sketch, "E369", {"start": v(21.46, 36.54) * mm, "end": v(22.26, 36.54) * mm});
            skLineSegment(sketch, "E370", {"start": v(22.26, 36.54) * mm, "end": v(22.26, 37.54) * mm});
            skLineSegment(sketch, "E371", {"start": v(22.26, 37.54) * mm, "end": v(36.26, 37.54) * mm});
            skLineSegment(sketch, "E372", {"start": v(36.26, 37.54) * mm, "end": v(36.26, 36.54) * mm});
            skLineSegment(sketch, "E373", {"start": v(36.26, 36.54) * mm, "end": v(37.06, 36.54) * mm});
            skLineSegment(sketch, "E374", {"start": v(37.06, 36.54) * mm, "end": v(37.06, 33.44) * mm});
            skLineSegment(sketch, "E375", {"start": v(37.06, 33.44) * mm, "end": v(36.26, 33.44) * mm});
            skLineSegment(sketch, "E376", {"start": v(36.26, 33.44) * mm, "end": v(36.26, 27.64) * mm});
            skLineSegment(sketch, "E377", {"start": v(36.26, 27.64) * mm, "end": v(37.06, 27.64) * mm});
            skLineSegment(sketch, "E378", {"start": v(37.06, 27.64) * mm, "end": v(37.06, 24.54) * mm});
            skLineSegment(sketch, "E379", {"start": v(37.06, 24.54) * mm, "end": v(36.26, 24.54) * mm});
            skLineSegment(sketch, "E380", {"start": v(36.26, 5.49) * mm, "end": v(36.26, 4.49) * mm});
            skLineSegment(sketch, "E381", {"start": v(36.26, 4.49) * mm, "end": v(22.26, 4.49) * mm});
            skLineSegment(sketch, "E382", {"start": v(22.26, 4.49) * mm, "end": v(22.26, 5.49) * mm});
            skLineSegment(sketch, "E383", {"start": v(22.26, 5.49) * mm, "end": v(21.46, 5.49) * mm});
            skLineSegment(sketch, "E384", {"start": v(21.46, 5.49) * mm, "end": v(21.46, 8.59) * mm});
            skLineSegment(sketch, "E385", {"start": v(21.46, 8.59) * mm, "end": v(22.26, 8.59) * mm});
            skLineSegment(sketch, "E386", {"start": v(22.26, 8.59) * mm, "end": v(22.26, 14.39) * mm});
            skLineSegment(sketch, "E387", {"start": v(22.26, 14.39) * mm, "end": v(21.46, 14.39) * mm});
            skLineSegment(sketch, "E388", {"start": v(21.46, 14.39) * mm, "end": v(21.46, 17.49) * mm});
            skLineSegment(sketch, "E389", {"start": v(21.46, 17.49) * mm, "end": v(22.26, 17.49) * mm});
            skLineSegment(sketch, "E390", {"start": v(22.26, 17.49) * mm, "end": v(22.26, 18.49) * mm});
            skLineSegment(sketch, "E391", {"start": v(22.26, 18.49) * mm, "end": v(36.26, 18.49) * mm});
            skLineSegment(sketch, "E392", {"start": v(36.26, 18.49) * mm, "end": v(36.26, 17.49) * mm});
            skLineSegment(sketch, "E393", {"start": v(36.26, 17.49) * mm, "end": v(37.06, 17.49) * mm});
            skLineSegment(sketch, "E394", {"start": v(37.06, 17.49) * mm, "end": v(37.06, 14.39) * mm});
            skLineSegment(sketch, "E395", {"start": v(37.06, 14.39) * mm, "end": v(36.26, 14.39) * mm});
            skLineSegment(sketch, "E396", {"start": v(36.26, 14.39) * mm, "end": v(36.26, 8.59) * mm});
            skLineSegment(sketch, "E397", {"start": v(36.26, 8.59) * mm, "end": v(37.06, 8.59) * mm});
            skLineSegment(sketch, "E398", {"start": v(37.06, 8.59) * mm, "end": v(37.06, 5.49) * mm});
            skLineSegment(sketch, "E399", {"start": v(37.06, 5.49) * mm, "end": v(36.26, 5.49) * mm});
            skLineSegment(sketch, "E400", {"start": v(55.3, 62.64) * mm, "end": v(55.3, 61.64) * mm});
            skLineSegment(sketch, "E401", {"start": v(55.3, 61.64) * mm, "end": v(41.3, 61.64) * mm});
            skLineSegment(sketch, "E402", {"start": v(41.3, 61.64) * mm, "end": v(41.3, 62.64) * mm});
            skLineSegment(sketch, "E403", {"start": v(41.3, 62.64) * mm, "end": v(40.5, 62.64) * mm});
            skLineSegment(sketch, "E404", {"start": v(40.5, 62.64) * mm, "end": v(40.5, 65.74) * mm});
            skLineSegment(sketch, "E405", {"start": v(40.5, 65.74) * mm, "end": v(41.3, 65.74) * mm});
            skLineSegment(sketch, "E406", {"start": v(41.3, 65.74) * mm, "end": v(41.3, 71.54) * mm});
            skLineSegment(sketch, "E407", {"start": v(41.3, 71.54) * mm, "end": v(40.5, 71.54) * mm});
            skLineSegment(sketch, "E408", {"start": v(40.5, 71.54) * mm, "end": v(40.5, 74.64) * mm});
            skLineSegment(sketch, "E409", {"start": v(40.5, 74.64) * mm, "end": v(41.3, 74.64) * mm});
            skLineSegment(sketch, "E410", {"start": v(41.3, 74.64) * mm, "end": v(41.3, 75.64) * mm});
            skLineSegment(sketch, "E411", {"start": v(41.3, 75.64) * mm, "end": v(55.3, 75.64) * mm});
            skLineSegment(sketch, "E412", {"start": v(55.3, 75.64) * mm, "end": v(55.3, 74.64) * mm});
            skLineSegment(sketch, "E413", {"start": v(55.3, 74.64) * mm, "end": v(56.1, 74.64) * mm});
            skLineSegment(sketch, "E414", {"start": v(56.1, 74.64) * mm, "end": v(56.1, 71.54) * mm});
            skLineSegment(sketch, "E415", {"start": v(56.1, 71.54) * mm, "end": v(55.3, 71.54) * mm});
            skLineSegment(sketch, "E416", {"start": v(55.3, 71.54) * mm, "end": v(55.3, 65.74) * mm});
            skLineSegment(sketch, "E417", {"start": v(55.3, 65.74) * mm, "end": v(56.1, 65.74) * mm});
            skLineSegment(sketch, "E418", {"start": v(56.1, 65.74) * mm, "end": v(56.1, 62.64) * mm});
            skLineSegment(sketch, "E419", {"start": v(56.1, 62.64) * mm, "end": v(55.3, 62.64) * mm});
            skLineSegment(sketch, "E420", {"start": v(55.3, 43.59) * mm, "end": v(55.3, 42.59) * mm});
            skLineSegment(sketch, "E421", {"start": v(55.3, 42.59) * mm, "end": v(41.3, 42.59) * mm});
            skLineSegment(sketch, "E422", {"start": v(41.3, 42.59) * mm, "end": v(41.3, 43.59) * mm});
            skLineSegment(sketch, "E423", {"start": v(41.3, 43.59) * mm, "end": v(40.5, 43.59) * mm});
            skLineSegment(sketch, "E424", {"start": v(40.5, 43.59) * mm, "end": v(40.5, 46.69) * mm});
            skLineSegment(sketch, "E425", {"start": v(40.5, 46.69) * mm, "end": v(41.3, 46.69) * mm});
            skLineSegment(sketch, "E426", {"start": v(41.3, 46.69) * mm, "end": v(41.3, 52.49) * mm});
            skLineSegment(sketch, "E427", {"start": v(41.3, 52.49) * mm, "end": v(40.5, 52.49) * mm});
            skLineSegment(sketch, "E428", {"start": v(40.5, 52.49) * mm, "end": v(40.5, 55.59) * mm});
            skLineSegment(sketch, "E429", {"start": v(40.5, 55.59) * mm, "end": v(41.3, 55.59) * mm});
            skLineSegment(sketch, "E430", {"start": v(41.3, 55.59) * mm, "end": v(41.3, 56.59) * mm});
            skLineSegment(sketch, "E431", {"start": v(41.3, 56.59) * mm, "end": v(55.3, 56.59) * mm});
            skLineSegment(sketch, "E432", {"start": v(55.3, 56.59) * mm, "end": v(55.3, 55.59) * mm});
            skLineSegment(sketch, "E433", {"start": v(55.3, 55.59) * mm, "end": v(56.1, 55.59) * mm});
            skLineSegment(sketch, "E434", {"start": v(56.1, 55.59) * mm, "end": v(56.1, 52.49) * mm});
            skLineSegment(sketch, "E435", {"start": v(56.1, 52.49) * mm, "end": v(55.3, 52.49) * mm});
            skLineSegment(sketch, "E436", {"start": v(55.3, 52.49) * mm, "end": v(55.3, 46.69) * mm});
            skLineSegment(sketch, "E437", {"start": v(55.3, 46.69) * mm, "end": v(56.1, 46.69) * mm});
            skLineSegment(sketch, "E438", {"start": v(56.1, 46.69) * mm, "end": v(56.1, 43.59) * mm});
            skLineSegment(sketch, "E439", {"start": v(56.1, 43.59) * mm, "end": v(55.3, 43.59) * mm});
            skLineSegment(sketch, "E440", {"start": v(55.3, 24.54) * mm, "end": v(55.3, 23.54) * mm});
            skLineSegment(sketch, "E441", {"start": v(55.3, 23.54) * mm, "end": v(41.3, 23.54) * mm});
            skLineSegment(sketch, "E442", {"start": v(41.3, 23.54) * mm, "end": v(41.3, 24.54) * mm});
            skLineSegment(sketch, "E443", {"start": v(41.3, 24.54) * mm, "end": v(40.5, 24.54) * mm});
            skLineSegment(sketch, "E444", {"start": v(40.5, 24.54) * mm, "end": v(40.5, 27.64) * mm});
            skLineSegment(sketch, "E445", {"start": v(40.5, 27.64) * mm, "end": v(41.3, 27.64) * mm});
            skLineSegment(sketch, "E446", {"start": v(41.3, 27.64) * mm, "end": v(41.3, 33.44) * mm});
            skLineSegment(sketch, "E447", {"start": v(41.3, 33.44) * mm, "end": v(40.5, 33.44) * mm});
            skLineSegment(sketch, "E448", {"start": v(40.5, 33.44) * mm, "end": v(40.5, 36.54) * mm});
            skLineSegment(sketch, "E449", {"start": v(40.5, 36.54) * mm, "end": v(41.3, 36.54) * mm});
            skLineSegment(sketch, "E450", {"start": v(41.3, 36.54) * mm, "end": v(41.3, 37.54) * mm});
            skLineSegment(sketch, "E451", {"start": v(41.3, 37.54) * mm, "end": v(55.3, 37.54) * mm});
            skLineSegment(sketch, "E452", {"start": v(55.3, 37.54) * mm, "end": v(55.3, 36.54) * mm});
            skLineSegment(sketch, "E453", {"start": v(55.3, 36.54) * mm, "end": v(56.1, 36.54) * mm});
            skLineSegment(sketch, "E454", {"start": v(56.1, 36.54) * mm, "end": v(56.1, 33.44) * mm});
            skLineSegment(sketch, "E455", {"start": v(56.1, 33.44) * mm, "end": v(55.3, 33.44) * mm});
            skLineSegment(sketch, "E456", {"start": v(55.3, 33.44) * mm, "end": v(55.3, 27.64) * mm});
            skLineSegment(sketch, "E457", {"start": v(55.3, 27.64) * mm, "end": v(56.1, 27.64) * mm});
            skLineSegment(sketch, "E458", {"start": v(56.1, 27.64) * mm, "end": v(56.1, 24.54) * mm});
            skLineSegment(sketch, "E459", {"start": v(56.1, 24.54) * mm, "end": v(55.3, 24.54) * mm});
            skLineSegment(sketch, "E460", {"start": v(55.3, 5.49) * mm, "end": v(55.3, 4.49) * mm});
            skLineSegment(sketch, "E461", {"start": v(55.3, 4.49) * mm, "end": v(41.3, 4.49) * mm});
            skLineSegment(sketch, "E462", {"start": v(41.3, 4.49) * mm, "end": v(41.3, 5.49) * mm});
            skLineSegment(sketch, "E463", {"start": v(41.3, 5.49) * mm, "end": v(40.5, 5.49) * mm});
            skLineSegment(sketch, "E464", {"start": v(40.5, 5.49) * mm, "end": v(40.5, 8.59) * mm});
            skLineSegment(sketch, "E465", {"start": v(40.5, 8.59) * mm, "end": v(41.3, 8.59) * mm});
            skLineSegment(sketch, "E466", {"start": v(41.3, 8.59) * mm, "end": v(41.3, 14.39) * mm});
            skLineSegment(sketch, "E467", {"start": v(41.3, 14.39) * mm, "end": v(40.5, 14.39) * mm});
            skLineSegment(sketch, "E468", {"start": v(40.5, 14.39) * mm, "end": v(40.5, 17.49) * mm});
            skLineSegment(sketch, "E469", {"start": v(40.5, 17.49) * mm, "end": v(41.3, 17.49) * mm});
            skLineSegment(sketch, "E470", {"start": v(41.3, 17.49) * mm, "end": v(41.3, 18.49) * mm});
            skLineSegment(sketch, "E471", {"start": v(41.3, 18.49) * mm, "end": v(55.3, 18.49) * mm});
            skLineSegment(sketch, "E472", {"start": v(55.3, 18.49) * mm, "end": v(55.3, 17.49) * mm});
            skLineSegment(sketch, "E473", {"start": v(55.3, 17.49) * mm, "end": v(56.1, 17.49) * mm});
            skLineSegment(sketch, "E474", {"start": v(56.1, 17.49) * mm, "end": v(56.1, 14.39) * mm});
            skLineSegment(sketch, "E475", {"start": v(56.1, 14.39) * mm, "end": v(55.3, 14.39) * mm});
            skLineSegment(sketch, "E476", {"start": v(55.3, 14.39) * mm, "end": v(55.3, 8.59) * mm});
            skLineSegment(sketch, "E477", {"start": v(55.3, 8.59) * mm, "end": v(56.1, 8.59) * mm});
            skLineSegment(sketch, "E478", {"start": v(56.1, 8.59) * mm, "end": v(56.1, 5.49) * mm});
            skLineSegment(sketch, "E479", {"start": v(56.1, 5.49) * mm, "end": v(55.3, 5.49) * mm});
            skLineSegment(sketch, "E480", {"start": v(56.84, 79.16) * mm, "end": v(57, 79.16) * mm});
            skLineSegment(sketch, "E481", {"start": v(57, 79.16) * mm, "end": v(57.15, 79.14) * mm});
            skLineSegment(sketch, "E482", {"start": v(57.15, 79.14) * mm, "end": v(57.3, 79.1) * mm});
            skLineSegment(sketch, "E483", {"start": v(57.3, 79.1) * mm, "end": v(57.45, 79.06) * mm});
            skLineSegment(sketch, "E484", {"start": v(57.45, 79.06) * mm, "end": v(57.6, 79.01) * mm});
            skLineSegment(sketch, "E485", {"start": v(57.6, 79.01) * mm, "end": v(57.74, 78.94) * mm});
            skLineSegment(sketch, "E486", {"start": v(57.74, 78.94) * mm, "end": v(57.88, 78.87) * mm});
            skLineSegment(sketch, "E487", {"start": v(57.88, 78.87) * mm, "end": v(58.01, 78.78) * mm});
            skLineSegment(sketch, "E488", {"start": v(58.01, 78.78) * mm, "end": v(58.13, 78.68) * mm});
            skLineSegment(sketch, "E489", {"start": v(58.13, 78.68) * mm, "end": v(58.25, 78.58) * mm});
            skLineSegment(sketch, "E490", {"start": v(58.25, 78.58) * mm, "end": v(58.36, 78.46) * mm});
            skLineSegment(sketch, "E491", {"start": v(58.36, 78.46) * mm, "end": v(58.45, 78.34) * mm});
            skLineSegment(sketch, "E492", {"start": v(58.45, 78.34) * mm, "end": v(58.54, 78.2) * mm});
            skLineSegment(sketch, "E493", {"start": v(58.54, 78.2) * mm, "end": v(58.62, 78.07) * mm});
            skLineSegment(sketch, "E494", {"start": v(58.62, 78.07) * mm, "end": v(58.68, 77.93) * mm});
            skLineSegment(sketch, "E495", {"start": v(58.68, 77.93) * mm, "end": v(58.74, 77.78) * mm});
            skLineSegment(sketch, "E496", {"start": v(58.74, 77.78) * mm, "end": v(58.78, 77.63) * mm});
            skLineSegment(sketch, "E497", {"start": v(58.78, 77.63) * mm, "end": v(58.8, 77.48) * mm});
            skLineSegment(sketch, "E498", {"start": v(58.8, 77.48) * mm, "end": v(58.83, 77.32) * mm});
            skLineSegment(sketch, "E499", {"start": v(58.83, 77.32) * mm, "end": v(58.83, 77.16) * mm});
            skLineSegment(sketch, "E500", {"start": v(58.83, 77.16) * mm, "end": v(58.83, -75.24) * mm});
            skLineSegment(sketch, "E501", {"start": v(58.83, -75.24) * mm, "end": v(58.83, -75.4) * mm});
            skLineSegment(sketch, "E502", {"start": v(58.83, -75.4) * mm, "end": v(58.8, -75.55) * mm});
            skLineSegment(sketch, "E503", {"start": v(58.8, -75.55) * mm, "end": v(58.78, -75.7) * mm});
            skLineSegment(sketch, "E504", {"start": v(58.78, -75.7) * mm, "end": v(58.74, -75.86) * mm});
            skLineSegment(sketch, "E505", {"start": v(58.74, -75.86) * mm, "end": v(58.68, -76) * mm});
            skLineSegment(sketch, "E506", {"start": v(58.68, -76) * mm, "end": v(58.62, -76.15) * mm});
            skLineSegment(sketch, "E507", {"start": v(58.62, -76.15) * mm, "end": v(58.54, -76.28) * mm});
            skLineSegment(sketch, "E508", {"start": v(58.54, -76.28) * mm, "end": v(58.45, -76.41) * mm});
            skLineSegment(sketch, "E509", {"start": v(58.45, -76.41) * mm, "end": v(58.36, -76.54) * mm});
            skLineSegment(sketch, "E510", {"start": v(58.36, -76.54) * mm, "end": v(58.25, -76.65) * mm});
            skLineSegment(sketch, "E511", {"start": v(58.25, -76.65) * mm, "end": v(58.13, -76.76) * mm});
            skLineSegment(sketch, "E512", {"start": v(58.13, -76.76) * mm, "end": v(58.01, -76.86) * mm});
            skLineSegment(sketch, "E513", {"start": v(58.01, -76.86) * mm, "end": v(57.88, -76.94) * mm});
            skLineSegment(sketch, "E514", {"start": v(57.88, -76.94) * mm, "end": v(57.74, -77.02) * mm});
            skLineSegment(sketch, "E515", {"start": v(57.74, -77.02) * mm, "end": v(57.6, -77.09) * mm});
            skLineSegment(sketch, "E516", {"start": v(57.6, -77.09) * mm, "end": v(57.45, -77.14) * mm});
            skLineSegment(sketch, "E517", {"start": v(57.45, -77.14) * mm, "end": v(57.3, -77.18) * mm});
            skLineSegment(sketch, "E518", {"start": v(57.3, -77.18) * mm, "end": v(57.15, -77.21) * mm});
            skLineSegment(sketch, "E519", {"start": v(57.15, -77.21) * mm, "end": v(57, -77.23) * mm});
            skLineSegment(sketch, "E520", {"start": v(57, -77.23) * mm, "end": v(56.84, -77.24) * mm});
            skLineSegment(sketch, "E521", {"start": v(56.84, -77.24) * mm, "end": v(-55.47, -77.24) * mm});
            skLineSegment(sketch, "E522", {"start": v(-55.47, -77.24) * mm, "end": v(-55.62, -77.23) * mm});
            skLineSegment(sketch, "E523", {"start": v(-55.62, -77.23) * mm, "end": v(-55.78, -77.21) * mm});
            skLineSegment(sketch, "E524", {"start": v(-55.78, -77.21) * mm, "end": v(-55.93, -77.18) * mm});
            skLineSegment(sketch, "E525", {"start": v(-55.93, -77.18) * mm, "end": v(-56.08, -77.14) * mm});
            skLineSegment(sketch, "E526", {"start": v(-56.08, -77.14) * mm, "end": v(-56.23, -77.09) * mm});
            skLineSegment(sketch, "E527", {"start": v(-56.23, -77.09) * mm, "end": v(-56.37, -77.02) * mm});
            skLineSegment(sketch, "E528", {"start": v(-56.37, -77.02) * mm, "end": v(-56.51, -76.94) * mm});
            skLineSegment(sketch, "E529", {"start": v(-56.51, -76.94) * mm, "end": v(-56.64, -76.86) * mm});
            skLineSegment(sketch, "E530", {"start": v(-56.64, -76.86) * mm, "end": v(-56.76, -76.76) * mm});
            skLineSegment(sketch, "E531", {"start": v(-56.76, -76.76) * mm, "end": v(-56.88, -76.65) * mm});
            skLineSegment(sketch, "E532", {"start": v(-56.88, -76.65) * mm, "end": v(-56.99, -76.54) * mm});
            skLineSegment(sketch, "E533", {"start": v(-56.99, -76.54) * mm, "end": v(-57.08, -76.41) * mm});
            skLineSegment(sketch, "E534", {"start": v(-57.08, -76.41) * mm, "end": v(-57.17, -76.28) * mm});
            skLineSegment(sketch, "E535", {"start": v(-57.17, -76.28) * mm, "end": v(-57.25, -76.15) * mm});
            skLineSegment(sketch, "E536", {"start": v(-57.25, -76.15) * mm, "end": v(-57.31, -76) * mm});
            skLineSegment(sketch, "E537", {"start": v(-57.31, -76) * mm, "end": v(-57.37, -75.86) * mm});
            skLineSegment(sketch, "E538", {"start": v(-57.37, -75.86) * mm, "end": v(-57.41, -75.7) * mm});
            skLineSegment(sketch, "E539", {"start": v(-57.41, -75.7) * mm, "end": v(-57.44, -75.55) * mm});
            skLineSegment(sketch, "E540", {"start": v(-57.44, -75.55) * mm, "end": v(-57.46, -75.4) * mm});
            skLineSegment(sketch, "E541", {"start": v(-57.46, -75.4) * mm, "end": v(-57.47, -75.24) * mm});
            skLineSegment(sketch, "E542", {"start": v(-57.47, -75.24) * mm, "end": v(-57.47, 77.16) * mm});
            skLineSegment(sketch, "E543", {"start": v(-57.47, 77.16) * mm, "end": v(-57.46, 77.32) * mm});
            skLineSegment(sketch, "E544", {"start": v(-57.46, 77.32) * mm, "end": v(-57.44, 77.48) * mm});
            skLineSegment(sketch, "E545", {"start": v(-57.44, 77.48) * mm, "end": v(-57.41, 77.63) * mm});
            skLineSegment(sketch, "E546", {"start": v(-57.41, 77.63) * mm, "end": v(-57.37, 77.78) * mm});
            skLineSegment(sketch, "E547", {"start": v(-57.37, 77.78) * mm, "end": v(-57.31, 77.93) * mm});
            skLineSegment(sketch, "E548", {"start": v(-57.31, 77.93) * mm, "end": v(-57.25, 78.07) * mm});
            skLineSegment(sketch, "E549", {"start": v(-57.25, 78.07) * mm, "end": v(-57.17, 78.2) * mm});
            skLineSegment(sketch, "E550", {"start": v(-57.17, 78.2) * mm, "end": v(-57.08, 78.34) * mm});
            skLineSegment(sketch, "E551", {"start": v(-57.08, 78.34) * mm, "end": v(-56.99, 78.46) * mm});
            skLineSegment(sketch, "E552", {"start": v(-56.99, 78.46) * mm, "end": v(-56.88, 78.58) * mm});
            skLineSegment(sketch, "E553", {"start": v(-56.88, 78.58) * mm, "end": v(-56.76, 78.68) * mm});
            skLineSegment(sketch, "E554", {"start": v(-56.76, 78.68) * mm, "end": v(-56.64, 78.78) * mm});
            skLineSegment(sketch, "E555", {"start": v(-56.64, 78.78) * mm, "end": v(-56.51, 78.87) * mm});
            skLineSegment(sketch, "E556", {"start": v(-56.51, 78.87) * mm, "end": v(-56.37, 78.94) * mm});
            skLineSegment(sketch, "E557", {"start": v(-56.37, 78.94) * mm, "end": v(-56.23, 79.01) * mm});
            skLineSegment(sketch, "E558", {"start": v(-56.23, 79.01) * mm, "end": v(-56.08, 79.06) * mm});
            skLineSegment(sketch, "E559", {"start": v(-56.08, 79.06) * mm, "end": v(-55.93, 79.1) * mm});
            skLineSegment(sketch, "E560", {"start": v(-55.93, 79.1) * mm, "end": v(-55.78, 79.14) * mm});
            skLineSegment(sketch, "E561", {"start": v(-55.78, 79.14) * mm, "end": v(-55.62, 79.16) * mm});
            skLineSegment(sketch, "E562", {"start": v(-55.62, 79.16) * mm, "end": v(-55.47, 79.16) * mm});
            skLineSegment(sketch, "E563", {"start": v(-55.47, 79.16) * mm, "end": v(56.84, 79.16) * mm});
            skSolve(sketch);
        }
        {
            var Q0;
            Q0=makeQuery(id+"F0.imprint","IMPRINT",FACE,{"disambiguationData":[TD([[makeQuery(id+"F0.imprint","IMPRINT",EDGE,{"derivedFrom":sQuery(id+"F0.wireOp",EDGE,"E0")}),1.0]])]});
            extrude(context, id + "F1", {"entities" : qUnion([Q0]), "depth" : 1.5 * mm});
        }
    });
